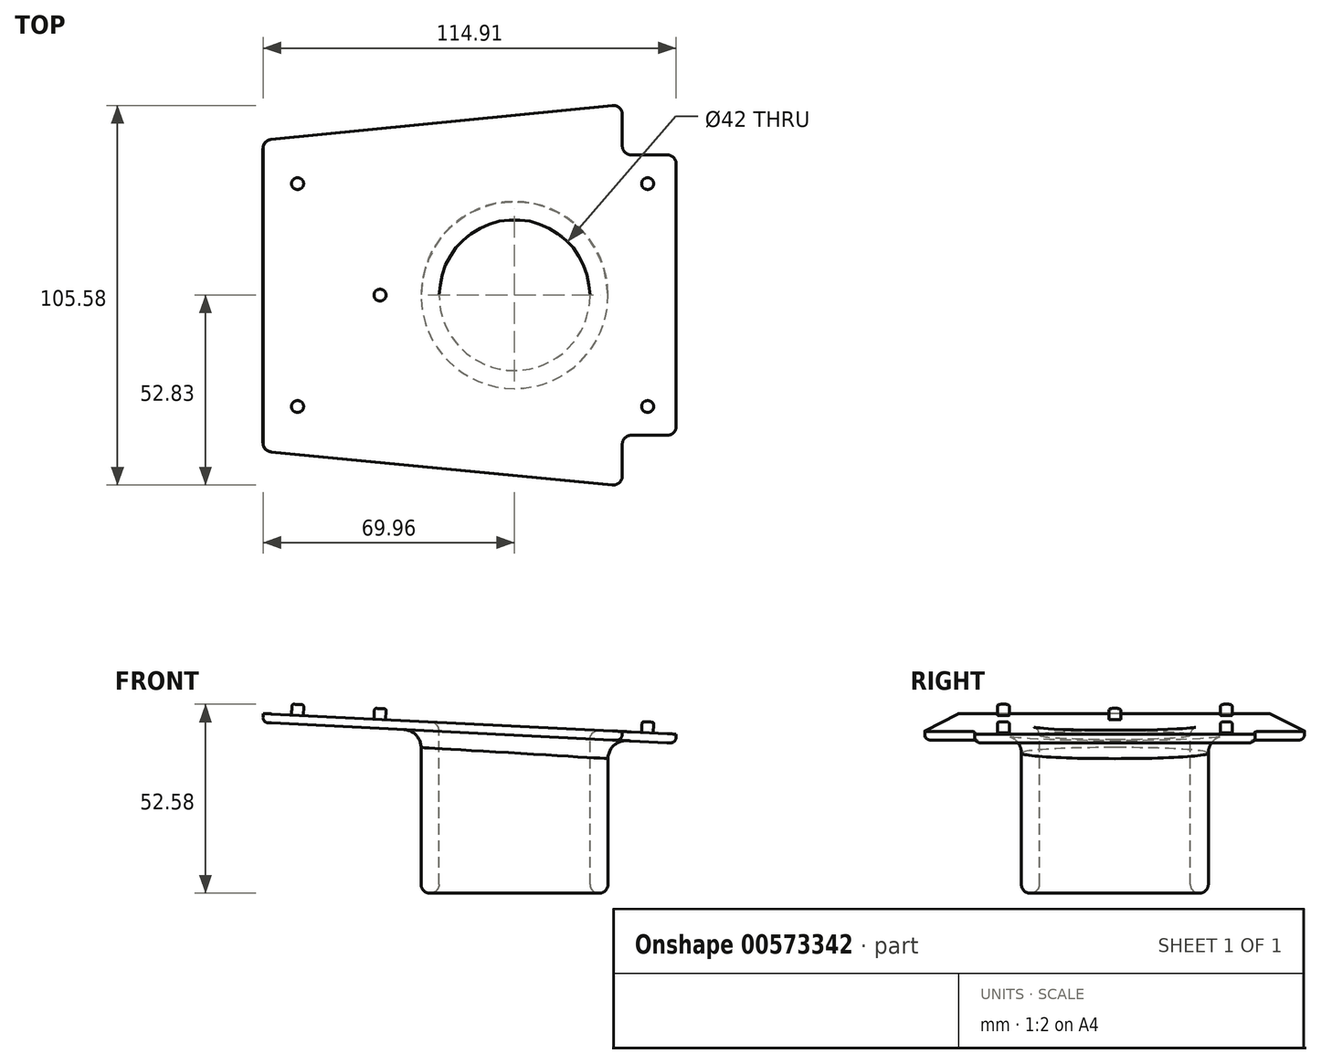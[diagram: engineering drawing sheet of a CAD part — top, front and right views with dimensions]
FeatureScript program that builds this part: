
annotation { "Feature Type Name" : "Feature", "Feature Type Description" : "" }
export const myFeature = defineFeature(function(context is Context, id is Id, definition is map)
    precondition{}
    {
        {
            var Q0;
            Q0=qCreatedBy(makeId("Right.planeOp"),FACE);
            var sketch = newSketch(context, id + "F0", { "sketchPlane" : qUnion([Q0])});
            skLineSegment(sketch, "E0", {"start": v(43, 0) * mm, "end": v(-43, 0) * mm});
            skSolve(sketch);
        }
        {
            var Q0;
            Q0=sQuery(id+"F0.wireOp",EDGE,"E0");
            cPlane(context, id + "F1", {"entities" : qUnion([Q0]), "cplaneType" : CPlaneType.LINE_ANGLE, "offset" : 25 * mm, "angle" : 2.86 * degree, "oppositeDirection" : true, "width" : 150 * mm, "height" : 150 * mm});
        }
        {
            var Q0;
            Q0=qCreatedBy(id+"F1.planeOp",FACE);
            var sketch = newSketch(context, id + "F2", { "sketchPlane" : qUnion([Q0])});
            skLineSegment(sketch, "E1", {"start": v(0, 0) * mm, "end": v(45, 0) * mm, "construction": true});
            skLineSegment(sketch, "E2", {"start": v(45, 0) * mm, "end": v(70, 0) * mm, "construction": true});
            skCircle(sketch, "E3", {"center": v(70, 0) * mm, "radius": 21 * mm, "construction": true});
            skCircle(sketch, "E4", {"center": v(70, 0) * mm, "radius": 26 * mm, "construction": true});
            skLineSegment(sketch, "E5", {"start": v(70, 0) * mm, "end": v(100, 0) * mm, "construction": true});
            skLineSegment(sketch, "E6", {"start": v(100, 0) * mm, "end": v(115, 0) * mm, "construction": true});
            skLineSegment(sketch, "E7", {"start": v(115, 0) * mm, "end": v(125, 0) * mm, "construction": true});
            skLineSegment(sketch, "E8", {"start": v(125, 0) * mm, "end": v(125, -55.5) * mm, "construction": true});
            skLineSegment(sketch, "E9.MirrorCS", {"start": v(125, 0) * mm, "end": v(125, 55.5) * mm, "construction": true});
            skLineSegment(sketch, "E10", {"start": v(125, 55.5) * mm, "end": v(0, 43.4) * mm, "construction": true});
            skLineSegment(sketch, "E11", {"start": v(125, -55.5) * mm, "end": v(0, -43.05) * mm, "construction": true});
            skLineSegment(sketch, "E12", {"start": v(100, 0) * mm, "end": v(100, -39) * mm, "construction": true});
            skLineSegment(sketch, "E13.MirrorCS", {"start": v(100, 0) * mm, "end": v(100, 39) * mm, "construction": true});
            skLineSegment(sketch, "E14", {"start": v(115, 0) * mm, "end": v(115, -39) * mm, "construction": true});
            skLineSegment(sketch, "E15.MirrorCS", {"start": v(115, 0) * mm, "end": v(115, 39) * mm, "construction": true});
            skLineSegment(sketch, "E16", {"start": v(0, 43.4) * mm, "end": v(100, 53.08) * mm});
            skLineSegment(sketch, "E17", {"start": v(100, 53.08) * mm, "end": v(100, 39) * mm});
            skLineSegment(sketch, "E18", {"start": v(100, 39) * mm, "end": v(115, 39) * mm});
            skLineSegment(sketch, "E19", {"start": v(115, 39) * mm, "end": v(115, -39) * mm});
            skLineSegment(sketch, "E20", {"start": v(115, -39) * mm, "end": v(100, -39) * mm});
            skLineSegment(sketch, "E21", {"start": v(100, -39) * mm, "end": v(100, -53.01) * mm});
            skLineSegment(sketch, "E22", {"start": v(100, -53.01) * mm, "end": v(0, -43.05) * mm});
            skLineSegment(sketch, "E23", {"start": v(0, -43.05) * mm, "end": v(0, 43.4) * mm});
            skSolve(sketch);
        }
        {
            var Q0;
            Q0 = qSketchRegion(id + "F2", true);
            extrude(context, id + "F3", {"entities" : qUnion([Q0]), "depth" : 2.5 * mm, "offsetDistance" : 25 * mm});
        }
        {
            var Q0;
            Q0=makeQuery(id+"F3.opExtrude","SWEPT_EDGE",EDGE,{"disambiguationData":[OSD([sQuery(id+"F2.wireOp",EDGE,"E16"),sQuery(id+"F2.wireOp",EDGE,"E23")])]});
            var Q1;
            Q1=makeQuery(id+"F3.opExtrude","SWEPT_EDGE",EDGE,{"disambiguationData":[OSD([sQuery(id+"F2.wireOp",EDGE,"E22"),sQuery(id+"F2.wireOp",EDGE,"E23")])]});
            var Q2;
            Q2=makeQuery(id+"F3.opExtrude","SWEPT_EDGE",EDGE,{"disambiguationData":[OSD([sQuery(id+"F2.wireOp",EDGE,"E19"),sQuery(id+"F2.wireOp",EDGE,"E20")])]});
            var Q3;
            Q3=makeQuery(id+"F3.opExtrude","SWEPT_EDGE",EDGE,{"disambiguationData":[OSD([sQuery(id+"F2.wireOp",EDGE,"E21"),sQuery(id+"F2.wireOp",EDGE,"E22")])]});
            var Q4;
            Q4=makeQuery(id+"F3.opExtrude","SWEPT_EDGE",EDGE,{"disambiguationData":[OSD([sQuery(id+"F2.wireOp",EDGE,"E20"),sQuery(id+"F2.wireOp",EDGE,"E21")])]});
            var Q5;
            Q5=makeQuery(id+"F3.opExtrude","SWEPT_EDGE",EDGE,{"disambiguationData":[OSD([sQuery(id+"F2.wireOp",EDGE,"E18"),sQuery(id+"F2.wireOp",EDGE,"E19")])]});
            var Q6;
            Q6=makeQuery(id+"F3.opExtrude","SWEPT_EDGE",EDGE,{"disambiguationData":[OSD([sQuery(id+"F2.wireOp",EDGE,"E16"),sQuery(id+"F2.wireOp",EDGE,"E17")])]});
            var Q7;
            Q7=makeQuery(id+"F3.opExtrude","SWEPT_EDGE",EDGE,{"disambiguationData":[OSD([sQuery(id+"F2.wireOp",EDGE,"E17"),sQuery(id+"F2.wireOp",EDGE,"E18")])]});
            fillet(context, id + "F4", {"entities" : qUnion([Q0, Q1, Q2, Q3, Q4, Q5, Q6, Q7]), "radius" : 2.5 * mm, "tangentPropagation" : true, "allowEdgeOverflow" : false});
        }
        {
            var Q0;
            Q0=makeQuery(id+"F3.opExtrude","CAP_EDGE",EDGE,{"disambiguationData":[OSD([sQuery(id+"F2.wireOp",EDGE,"E19")])],"isStart":false});
            var Q1;
            Q1=makeQuery(id+"F3.opExtrude","CAP_EDGE",EDGE,{"disambiguationData":[OSD([sQuery(id+"F2.wireOp",EDGE,"E23")])],"isStart":false});
            var Q2;
            Q2=makeQuery(id+"F3.opExtrude","CAP_EDGE",EDGE,{"disambiguationData":[OSD([sQuery(id+"F2.wireOp",EDGE,"E17")])],"isStart":false});
            var Q3;
            Q3=makeQuery(id+"F3.opExtrude","CAP_EDGE",EDGE,{"disambiguationData":[OSD([sQuery(id+"F2.wireOp",EDGE,"E21")])],"isStart":false});
            var Q4;
            Q4=makeQuery(id+"F3.opExtrude","CAP_EDGE",EDGE,{"disambiguationData":[OSD([sQuery(id+"F2.wireOp",EDGE,"E22")])],"isStart":false});
            var Q5;
            Q5=makeQuery(id+"F3.opExtrude","CAP_EDGE",EDGE,{"disambiguationData":[OSD([sQuery(id+"F2.wireOp",EDGE,"E16")])],"isStart":false});
            var Q6;
            Q6=makeQuery(id+"F3.opExtrude","CAP_EDGE",EDGE,{"disambiguationData":[OSD([sQuery(id+"F2.wireOp",EDGE,"E18")])],"isStart":false});
            var Q7;
            Q7=makeQuery(id+"F3.opExtrude","CAP_EDGE",EDGE,{"disambiguationData":[OSD([sQuery(id+"F2.wireOp",EDGE,"E20")])],"isStart":false});
            fillet(context, id + "F5", {"entities" : qUnion([Q0, Q1, Q2, Q3, Q4, Q5, Q6, Q7]), "radius" : 1.5 * mm, "allowEdgeOverflow" : false});
        }
        {
            var Q0;
            Q0=qCreatedBy(makeId("Top.planeOp"),FACE);
            var sketch = newSketch(context, id + "F6", { "sketchPlane" : qUnion([Q0])});
            skLineSegment(sketch, "E24", {"start": v(0, 0) * mm, "end": v(69.9, 0) * mm, "construction": true});
            skCircle(sketch, "E25", {"center": v(69.9, 0) * mm, "radius": 26 * mm});
            skCircle(sketch, "E26", {"center": v(69.9, 0) * mm, "radius": 21 * mm});
            skSolve(sketch);
        }
        {
            var Q0;
            Q0 = qSketchRegion(id + "F6", true);
            extrude(context, id + "F7", {"entities" : qUnion([Q0]), "oppositeDirection" : true, "depth" : 50 * mm, "offsetDistance" : 25 * mm});
        }
        {
            var Q0;
            Q0=makeQuery(id+"F3.opExtrude","SWEPT_BODY",BODY,{"disambiguationData":[OSD([sQuery(id+"F2.wireOp",EDGE,"E16"),sQuery(id+"F2.wireOp",EDGE,"E17"),sQuery(id+"F2.wireOp",EDGE,"E18"),sQuery(id+"F2.wireOp",EDGE,"E19"),sQuery(id+"F2.wireOp",EDGE,"E20"),sQuery(id+"F2.wireOp",EDGE,"E21"),sQuery(id+"F2.wireOp",EDGE,"E22"),sQuery(id+"F2.wireOp",EDGE,"E23")])]});
            var Q1;
            Q1=makeQuery(id+"F7.opExtrude","SWEPT_BODY",BODY,{"disambiguationData":[OSD([sQuery(id+"F6.wireOp",EDGE,"E25"),sQuery(id+"F6.wireOp",EDGE,"E26")])]});
            booleanBodies(context, id + "F8", {"operationType" : BooleanOperationType.UNION, "tools" : qUnion([Q0, Q1])});
        }
        {
            var Q0;
            Q0=makeQuery(id+"F6.imprint","IMPRINT",FACE,{"disambiguationData":[TD([[makeQuery(id+"F6.imprint","IMPRINT",EDGE,{"derivedFrom":sQuery(id+"F6.wireOp",EDGE,"E26")}),1.0]])]});
            extrude(context, id + "F9", {"entities" : qUnion([Q0]), "operationType" : NewBodyOperationType.REMOVE, "oppositeDirection" : true, "depth" : 10 * mm, "offsetDistance" : 25 * mm});
        }
        {
            var Q0;
            {var subQ0=sQuery(id+"F2.wireOp",EDGE,"E23");var subQ1=sQuery(id+"F2.wireOp",EDGE,"E16");var subQ2=sQuery(id+"F2.wireOp",EDGE,"E22");var subQ3=sQuery(id+"F2.wireOp",EDGE,"E21");var subQ4=sQuery(id+"F2.wireOp",EDGE,"E20");var subQ5=sQuery(id+"F2.wireOp",EDGE,"E17");var subQ6=sQuery(id+"F2.wireOp",EDGE,"E19");var subQ7=sQuery(id+"F2.wireOp",EDGE,"E18");Q0=makeQuery(id+"F8.opBoolean","SPLIT",FACE,{"disambiguationData":[TD([makeQuery(id+"F3.opExtrude","SWEPT_FACE",FACE,{"disambiguationData":[OSD([subQ1])]})])],"derivedFrom":makeQuery(id+"F3.opExtrude","CAP_FACE",FACE,{"disambiguationData":[OSD([subQ1,subQ5,subQ7,subQ6,subQ4,subQ3,subQ2,subQ0])],"isStart":true})});}
            var sketch = newSketch(context, id + "F10", { "sketchPlane" : qUnion([Q0])});
            skEllipse(sketch, "E27", {"center": v(70, 0) * mm, "majorRadius": 26.5 * mm, "minorRadius": 26.06 * mm, "majorAxis": v(-1, 0)});
            skSolve(sketch);
        }
        {
            var Q0;
            Q0 = qSketchRegion(id + "F10", true);
            extrude(context, id + "F11", {"entities" : qUnion([Q0]), "operationType" : NewBodyOperationType.REMOVE, "depth" : 17 * mm, "offsetDistance" : 25 * mm});
        }
        {
            var Q0;
            Q0=makeQuery(id+"F7.opExtrude","CAP_EDGE",EDGE,{"disambiguationData":[OSD([sQuery(id+"F6.wireOp",EDGE,"E25")])],"isStart":false});
            var Q1;
            Q1=makeQuery(id+"F7.opExtrude","CAP_EDGE",EDGE,{"disambiguationData":[OSD([sQuery(id+"F6.wireOp",EDGE,"E26")])],"isStart":false});
            var Q2;
            {var subQ0=sQuery(id+"F6.wireOp",EDGE,"E26");var subQ9=sQuery(id+"F6.wireOp",EDGE,"E25");var subQ10=makeQuery(id+"F7.opExtrude","SWEPT_FACE",FACE,{"disambiguationData":[OSD([subQ0])]});Q2=makeQuery(id+"F11.boolean.opBoolean","INTERSECT",EDGE,{"derivedFrom":[makeQuery(id+"F9.boolean.opBoolean","MERGE",FACE,{"derivedFrom":[makeQuery(id+"F8.opBoolean","SPLIT",FACE,{"disambiguationData":[TD([makeQuery(id+"F7.opExtrude","CAP_FACE",FACE,{"disambiguationData":[OSD([subQ9,subQ0])],"isStart":true})])],"derivedFrom":subQ10}),makeQuery(id+"F8.opBoolean","SPLIT",FACE,{"disambiguationData":[TD([makeQuery(id+"F7.opExtrude","CAP_FACE",FACE,{"disambiguationData":[OSD([subQ9,subQ0])],"isStart":false})])],"derivedFrom":subQ10}),makeQuery(id+"F9.opExtrude","SWEPT_FACE",FACE,{"disambiguationData":[OSD([subQ0])]})]}),makeQuery(id+"F11.opExtrude","CAP_FACE",FACE,{"disambiguationData":[OSD([sQuery(id+"F10.wireOp",EDGE,"E27")])],"isStart":true})]});}
            fillet(context, id + "F12", {"entities" : qUnion([Q0, Q1, Q2]), "radius" : 2.5 * mm, "allowEdgeOverflow" : false});
        }
        {
            var Q0;
            Q0=makeQuery(id+"F8.opBoolean","INTERSECT",EDGE,{"derivedFrom":[makeQuery(id+"F3.opExtrude","CAP_FACE",FACE,{"disambiguationData":[OSD([sQuery(id+"F2.wireOp",EDGE,"E16"),sQuery(id+"F2.wireOp",EDGE,"E17"),sQuery(id+"F2.wireOp",EDGE,"E18"),sQuery(id+"F2.wireOp",EDGE,"E19"),sQuery(id+"F2.wireOp",EDGE,"E20"),sQuery(id+"F2.wireOp",EDGE,"E21"),sQuery(id+"F2.wireOp",EDGE,"E22"),sQuery(id+"F2.wireOp",EDGE,"E23")])],"isStart":false}),makeQuery(id+"F7.opExtrude","SWEPT_FACE",FACE,{"disambiguationData":[OSD([sQuery(id+"F6.wireOp",EDGE,"E25")])]})]});
            fillet(context, id + "F13", {"entities" : qUnion([Q0]), "radius" : 5 * mm, "tangentPropagation" : true, "allowEdgeOverflow" : false});
        }
        {
            var Q0;
            {var subQ0=sQuery(id+"F2.wireOp",EDGE,"E23");var subQ1=sQuery(id+"F2.wireOp",EDGE,"E16");var subQ2=sQuery(id+"F2.wireOp",EDGE,"E22");var subQ3=sQuery(id+"F2.wireOp",EDGE,"E21");var subQ4=sQuery(id+"F2.wireOp",EDGE,"E20");var subQ5=sQuery(id+"F2.wireOp",EDGE,"E17");var subQ6=sQuery(id+"F2.wireOp",EDGE,"E19");var subQ7=sQuery(id+"F2.wireOp",EDGE,"E18");Q0=makeQuery(id+"F11.boolean.opBoolean","MERGE",FACE,{"derivedFrom":[makeQuery(id+"F8.opBoolean","SPLIT",FACE,{"disambiguationData":[TD([makeQuery(id+"F3.opExtrude","SWEPT_FACE",FACE,{"disambiguationData":[OSD([subQ1])]})])],"derivedFrom":makeQuery(id+"F3.opExtrude","CAP_FACE",FACE,{"disambiguationData":[OSD([subQ1,subQ5,subQ7,subQ6,subQ4,subQ3,subQ2,subQ0])],"isStart":true})}),makeQuery(id+"F11.opExtrude","CAP_FACE",FACE,{"disambiguationData":[OSD([sQuery(id+"F10.wireOp",EDGE,"E27")])],"isStart":true})]});}
            var sketch = newSketch(context, id + "F14", { "sketchPlane" : qUnion([Q0])});
            skPoint(sketch, "E28", {"position": v(115, 39) * mm});
            skLineSegment(sketch, "E29.bottom", {"start": v(115, 39) * mm, "end": v(107, 39) * mm, "construction": true});
            skLineSegment(sketch, "E29.top", {"start": v(115, 31) * mm, "end": v(107, 31) * mm, "construction": true});
            skLineSegment(sketch, "E29.left", {"start": v(115, 39) * mm, "end": v(115, 31) * mm, "construction": true});
            skLineSegment(sketch, "E29.right", {"start": v(107, 39) * mm, "end": v(107, 31) * mm, "construction": true});
            skLineSegment(sketch, "E30", {"start": v(115, 0) * mm, "end": v(107.76, 0) * mm, "construction": true});
            skPoint(sketch, "E30.endSnap0", {"position": v(115, 0) * mm});
            skCircle(sketch, "E31", {"center": v(107, 31) * mm, "radius": 1.63 * mm});
            skCircle(sketch, "E32.MirrorC", {"center": v(107, -31) * mm, "radius": 1.63 * mm});
            skLineSegment(sketch, "E33", {"start": v(107.76, 0) * mm, "end": v(58.26, 0) * mm, "construction": true});
            skPoint(sketch, "E33.endSnap0", {"position": v(46.6, 0) * mm});
            skLineSegment(sketch, "E34", {"start": v(58.26, 0) * mm, "end": v(58.26, -8) * mm, "construction": true});
            skCircle(sketch, "E35.MirrorC", {"center": v(9.52, 31) * mm, "radius": 1.63 * mm});
            skCircle(sketch, "E36.MirrorC", {"center": v(9.52, -31) * mm, "radius": 1.63 * mm});
            skLineSegment(sketch, "E37", {"start": v(46.6, 0) * mm, "end": v(32.48, 0) * mm, "construction": true});
            skCircle(sketch, "E38", {"center": v(32.48, 0) * mm, "radius": 1.63 * mm});
            skSolve(sketch);
        }
        {
            var Q0;
            Q0 = qSketchRegion(id + "F14", true);
            extrude(context, id + "F15", {"entities" : qUnion([Q0]), "operationType" : NewBodyOperationType.ADD, "depth" : 3 * mm, "offsetDistance" : 25 * mm});
        }
        {
            var Q0;
            Q0=makeQuery(id+"F15.opExtrude","CAP_EDGE",EDGE,{"disambiguationData":[OSD([sQuery(id+"F14.wireOp",EDGE,"E31")])],"isStart":false});
            var Q1;
            Q1=makeQuery(id+"F15.opExtrude","CAP_EDGE",EDGE,{"disambiguationData":[OSD([sQuery(id+"F14.wireOp",EDGE,"E32.MirrorC")])],"isStart":false});
            var Q2;
            Q2=makeQuery(id+"F15.opExtrude","CAP_EDGE",EDGE,{"disambiguationData":[OSD([sQuery(id+"F14.wireOp",EDGE,"E38")])],"isStart":false});
            var Q3;
            Q3=makeQuery(id+"F15.opExtrude","CAP_EDGE",EDGE,{"disambiguationData":[OSD([sQuery(id+"F14.wireOp",EDGE,"E35.MirrorC")])],"isStart":false});
            var Q4;
            Q4=makeQuery(id+"F15.opExtrude","CAP_EDGE",EDGE,{"disambiguationData":[OSD([sQuery(id+"F14.wireOp",EDGE,"E36.MirrorC")])],"isStart":false});
            fillet(context, id + "F16", {"entities" : qUnion([Q0, Q1, Q2, Q3, Q4]), "radius" : .5 * mm, "tangentPropagation" : true, "allowEdgeOverflow" : false});
        }
    });
